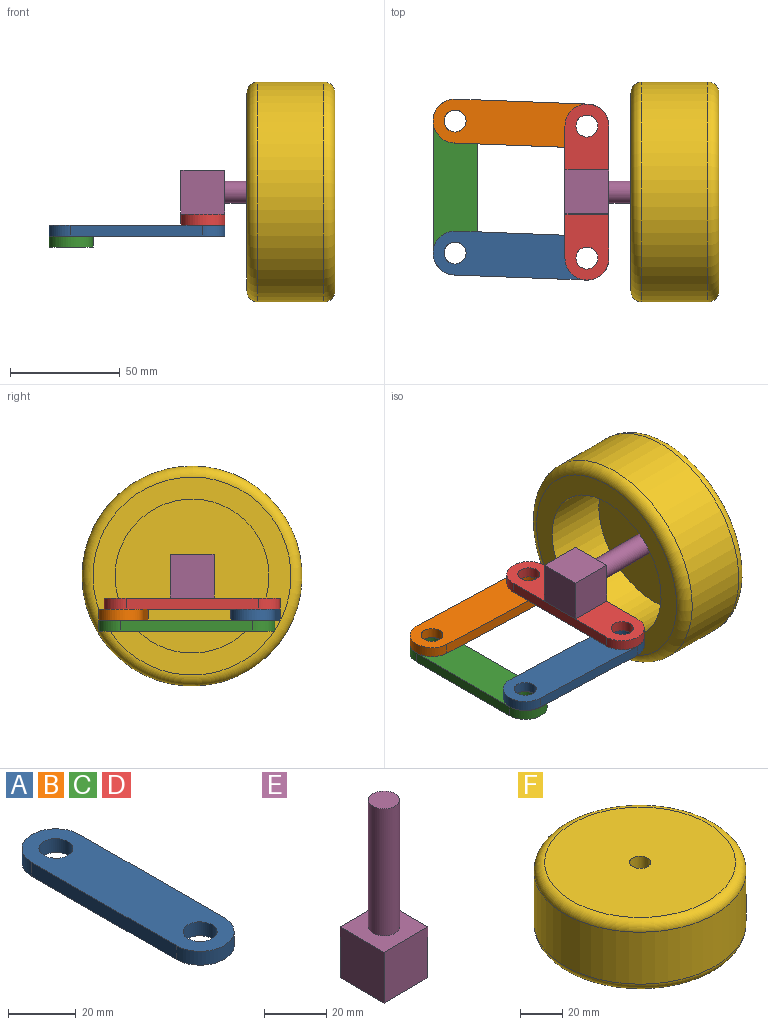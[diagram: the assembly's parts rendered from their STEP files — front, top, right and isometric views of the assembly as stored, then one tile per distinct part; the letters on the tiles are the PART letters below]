
ASSEMBLY  parts=6 mates=6
PART A: 8 faces, bbox 20x80x5 mm
  f0: plane 60x5mm, normal (-1,0,0), area 300mm2, adj f4,f5,f6,f7
  f1: plane 60x5mm, normal (1,0,0), area 300mm2, adj f4,f5,f6,f7
  f2: cylinder r=5mm len=10mm, axis (0,0,-1), area 157.1mm2, adj f4,f5
  f3: cylinder r=5mm len=10mm, axis (0,0,-1), area 157.1mm2, adj f4,f5
  f4: plane 80x20mm, normal (0,0,1), area 1357.1mm2, adj f0,f1,f2,f3,f6,f7
  f5: plane 80x20mm, normal (0,0,-1), area 1357.1mm2, adj f0,f1,f2,f3,f6,f7
  f6: cylinder r=10mm len=20mm, axis (0,0,-1), area 157.1mm2, adj f0,f1,f4,f5
  f7: cylinder r=10mm len=20mm, axis (0,0,-1), area 157.1mm2, adj f0,f1,f4,f5
PART B: same geometry as A
PART C: same geometry as A
PART D: same geometry as A
PART E: 8 faces, bbox 20x20x70 mm
  f0: plane 20x20mm, normal (-1,0,0), area 400mm2, adj f1,f3,f4,f5
  f1: plane 20x20mm, normal (0,-1,0), area 400mm2, adj f0,f2,f4,f5
  f2: plane 20x20mm, normal (1,0,0), area 400mm2, adj f1,f3,f4,f5
  f3: plane 20x20mm, normal (0,1,0), area 400mm2, adj f0,f2,f4,f5
  f4: plane 20x20mm, normal (0,0,1), area 321.5mm2, adj f0,f1,f2,f3,f6
  f5: plane 20x20mm, normal (0,0,-1), area 400mm2, adj f0,f1,f2,f3
  f6: cylinder r=5mm len=50mm, axis (0,0,-1), area 1570.8mm2, adj f4,f7
  f7: plane 10x10mm, normal (0,0,1), area 78.5mm2, adj f6
PART F: 8 faces, bbox 108.2x108.2x40 mm
  f0: cylinder r=5mm len=10mm, axis (0,0,-1), area 314.2mm2, adj f2,f5
  f1: cylinder r=50mm len=100mm, axis (0,0,-1), area 9424.8mm2, adj f6,f7
  f2: plane 90x90mm, normal (0,0,1), area 6283.2mm2, adj f0,f7
  f3: plane 90x90mm, normal (0,0,-1), area 2513.3mm2, adj f4,f6
  f4: cylinder r=35mm len=70mm, axis (0,0,-1), area 6597.3mm2, adj f3,f5
  f5: plane 70x70mm, normal (0,0,-1), area 3769.9mm2, adj f0,f4
  f6: torus R=45mm, axis (0,0,1), area 2377.7mm2, adj f1,f3
  f7: torus R=45mm, axis (0,0,1), area 2377.7mm2, adj f1,f2
PLACE A rot(axis=(0,0,1),87.8deg) t=(-35.16,-53.33,25.64)mm
PLACE B rot(axis=(0,0,1),87.8deg) t=(-35.16,6.67,25.64)mm
PLACE C t=(-65.13,-22.18,20.64)mm fixed
PLACE D rot(axis=(0,0,1),180deg) t=(-5.18,-24.49,30.64)mm
PLACE E rot(axis=(0,1,0),90deg) t=(-15.18,-24.49,45.64)mm
PLACE F rot(axis=(-0.7,0.09,-0.7),169.5deg) t=(14.82,-24.49,45.64)mm
MATE revolute C.f2 <-> B.f2  axis (0,0,1) through (-65.13,7.82,25.64)mm
MATE fastened E.f2 <-> D.f4  axis (0,0,-1) through (-5.18,-24.49,35.64)mm
MATE revolute B.f3 <-> D.f3  axis (0,0,1) through (-5.18,5.51,30.64)mm
MATE revolute A.f3 <-> D.f2  axis (0,0,1) through (-5.18,-54.49,30.64)mm
MATE revolute E.f6 <-> F.f0  axis (-1,0,0) through (54.82,-24.49,45.64)mm
MATE revolute C.f3 <-> A.f2  axis (0,0,1) through (-65.13,-52.18,25.64)mm
